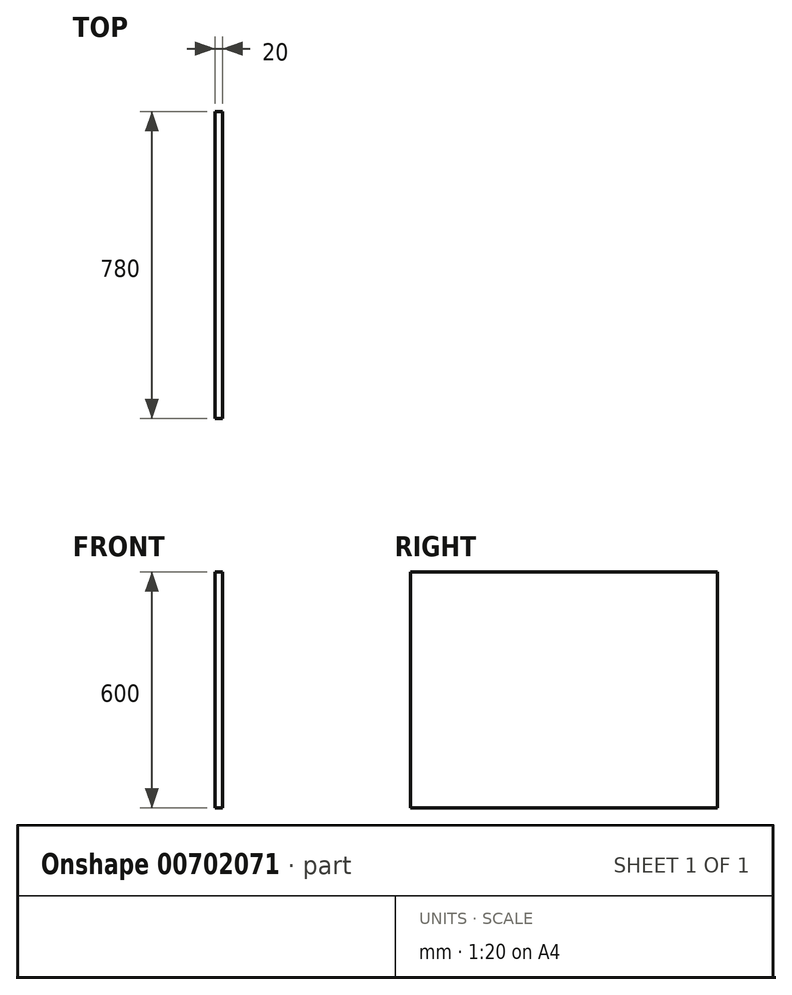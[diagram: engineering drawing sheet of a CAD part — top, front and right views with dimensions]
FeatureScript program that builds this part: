
annotation { "Feature Type Name" : "Feature", "Feature Type Description" : "" }
export const myFeature = defineFeature(function(context is Context, id is Id, definition is map)
    precondition{}
    {
        {
            var Q0;
            Q0=qCreatedBy(makeId("Right.planeOp"),FACE);
            var sketch = newSketch(context, id + "F0", { "sketchPlane" : qUnion([Q0])});
            skLineSegment(sketch, "E0.bottom", {"start": v(0, 0) * mm, "end": v(780, 0) * mm});
            skLineSegment(sketch, "E0.top", {"start": v(0, 600) * mm, "end": v(780, 600) * mm});
            skLineSegment(sketch, "E0.left", {"start": v(0, 0) * mm, "end": v(0, 600) * mm});
            skLineSegment(sketch, "E0.right", {"start": v(780, 0) * mm, "end": v(780, 600) * mm});
            skSolve(sketch);
        }
        {
            var Q0;
            Q0=qSketchRegion(id+"F0",true);
            extrude(context, id + "F1", {"entities" : qUnion([Q0]), "depth" : 20 * mm, "offsetDistance" : 25 * mm});
        }
    });
